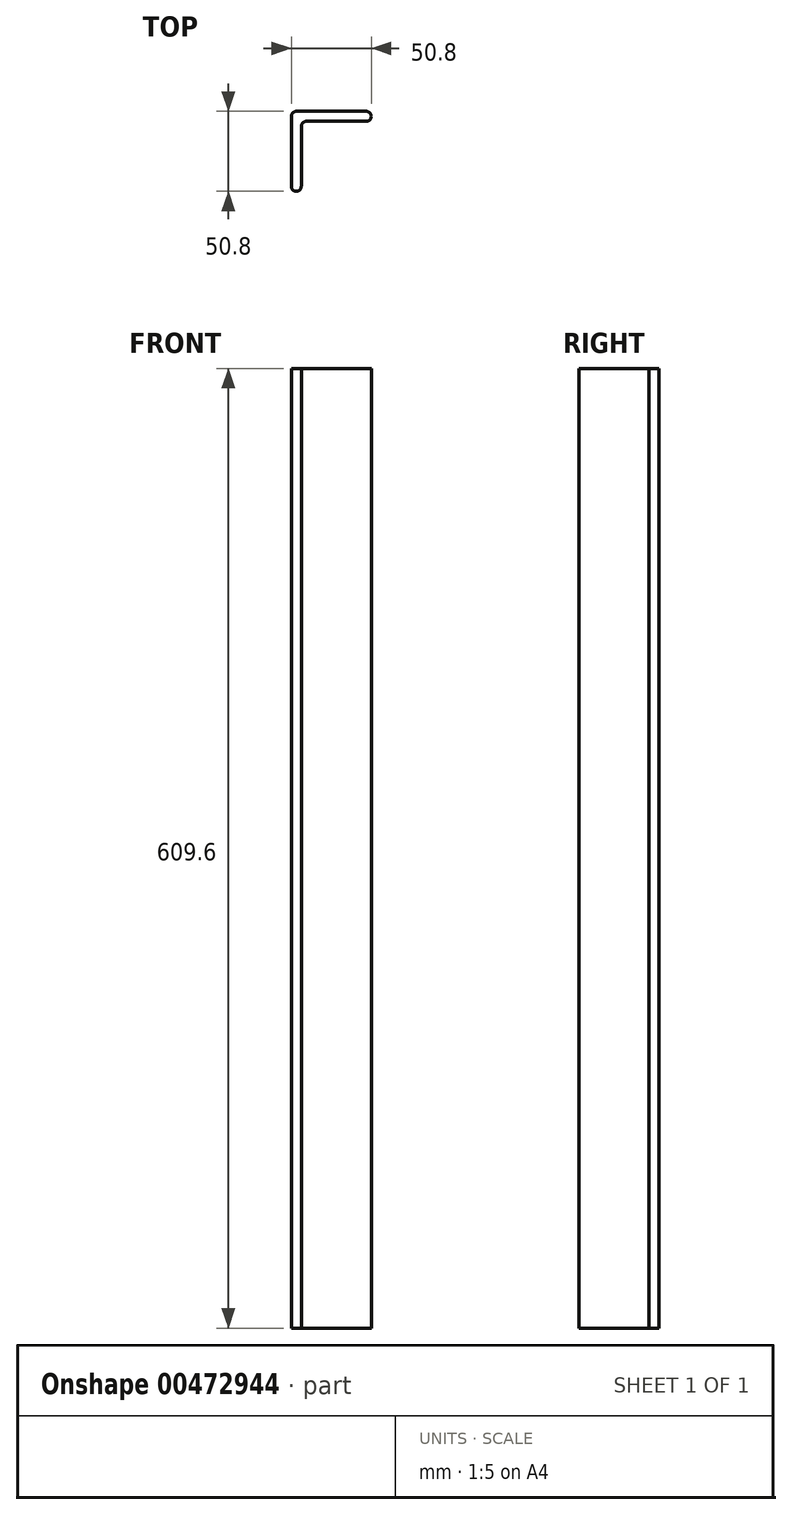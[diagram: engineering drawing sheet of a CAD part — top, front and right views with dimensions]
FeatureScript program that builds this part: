
annotation { "Feature Type Name" : "Feature", "Feature Type Description" : "" }
export const myFeature = defineFeature(function(context is Context, id is Id, definition is map)
    precondition{}
    {
        {
            var Q0;
            Q0=qCreatedBy(makeId("Top.planeOp"),FACE);
            var sketch = newSketch(context, id + "F0", { "sketchPlane" : qUnion([Q0])});
            skLineSegment(sketch, "E0", {"start": v(0, -28.6) * mm, "end": v(0, 22.2) * mm});
            skLineSegment(sketch, "E1", {"start": v(0, 22.2) * mm, "end": v(50.8, 22.2) * mm});
            skLineSegment(sketch, "E2", {"start": v(50.8, 22.2) * mm, "end": v(50.8, 15.86) * mm});
            skLineSegment(sketch, "E3", {"start": v(50.8, 15.86) * mm, "end": v(6.35, 15.86) * mm});
            skLineSegment(sketch, "E4", {"start": v(6.35, 15.86) * mm, "end": v(6.35, -28.6) * mm});
            skLineSegment(sketch, "E5", {"start": v(6.35, -28.6) * mm, "end": v(0, -28.6) * mm});
            skSolve(sketch);
        }
        {
            var Q0;
            Q0=makeQuery(id+"F0.imprint","IMPRINT",FACE,{"disambiguationData":[TD([[makeQuery(id+"F0.imprint","IMPRINT",EDGE,{"derivedFrom":sQuery(id+"F0.wireOp",EDGE,"E0")}),-1.0]])]});
            extrude(context, id + "F1", {"entities" : qUnion([Q0]), "depth" : 609.6 * mm});
        }
        {
            var Q0;
            Q0=makeQuery(id+"F1.opExtrude","SWEPT_EDGE",EDGE,{"disambiguationData":[OSD([sQuery(id+"F0.wireOp",EDGE,"E0"),sQuery(id+"F0.wireOp",EDGE,"E5")])]});
            var Q1;
            Q1=makeQuery(id+"F1.opExtrude","SWEPT_EDGE",EDGE,{"disambiguationData":[OSD([sQuery(id+"F0.wireOp",EDGE,"E4"),sQuery(id+"F0.wireOp",EDGE,"E5")])]});
            var Q2;
            Q2=makeQuery(id+"F1.opExtrude","SWEPT_EDGE",EDGE,{"disambiguationData":[OSD([sQuery(id+"F0.wireOp",EDGE,"E3"),sQuery(id+"F0.wireOp",EDGE,"E4")])]});
            var Q3;
            Q3=makeQuery(id+"F1.opExtrude","SWEPT_EDGE",EDGE,{"disambiguationData":[OSD([sQuery(id+"F0.wireOp",EDGE,"E2"),sQuery(id+"F0.wireOp",EDGE,"E3")])]});
            var Q4;
            Q4=makeQuery(id+"F1.opExtrude","SWEPT_EDGE",EDGE,{"disambiguationData":[OSD([sQuery(id+"F0.wireOp",EDGE,"E1"),sQuery(id+"F0.wireOp",EDGE,"E2")])]});
            var Q5;
            Q5=makeQuery(id+"F1.opExtrude","SWEPT_EDGE",EDGE,{"disambiguationData":[OSD([sQuery(id+"F0.wireOp",EDGE,"E0"),sQuery(id+"F0.wireOp",EDGE,"E1")])]});
            fillet(context, id + "F2", {"entities" : qUnion([Q0, Q1, Q2, Q3, Q4, Q5]), "radius" : 3.17 * mm, "tangentPropagation" : true, "allowEdgeOverflow" : false});
        }
    });
